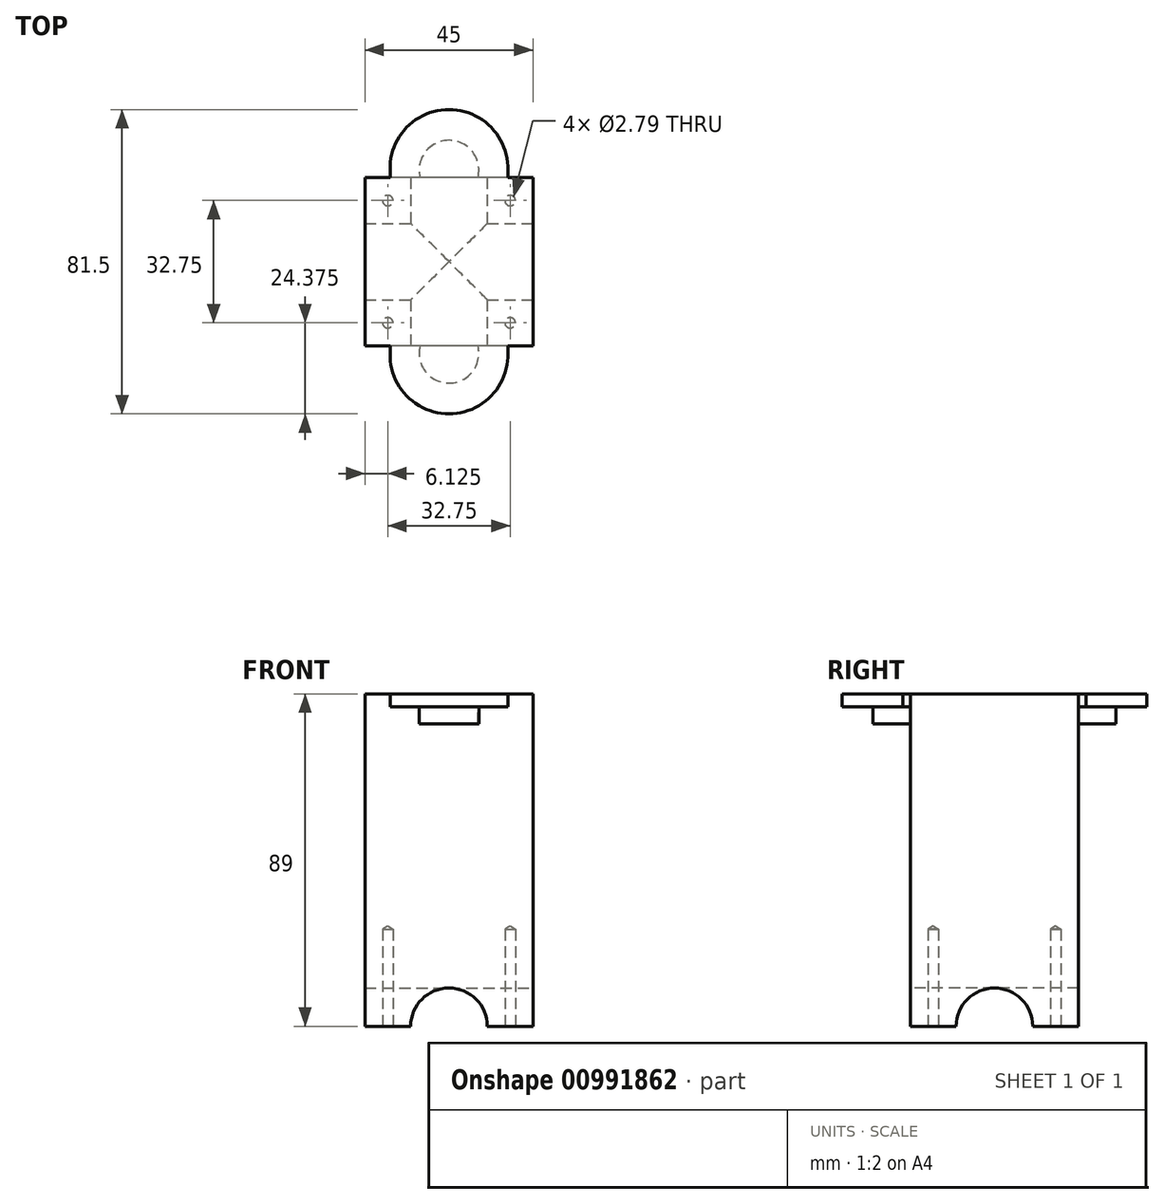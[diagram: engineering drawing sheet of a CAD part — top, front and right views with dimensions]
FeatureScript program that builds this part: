
annotation { "Feature Type Name" : "Feature", "Feature Type Description" : "" }
export const myFeature = defineFeature(function(context is Context, id is Id, definition is map)
    precondition{}
    {
        {
            var Q0;
            Q0=qCreatedBy(makeId("Top.planeOp"),FACE);
            var sketch = newSketch(context, id + "F0", { "sketchPlane" : qUnion([Q0])});
            skLineSegment(sketch, "E0.bottom", {"start": v(22.5, -22.5) * mm, "end": v(-22.5, -22.5) * mm});
            skLineSegment(sketch, "E0.top", {"start": v(22.5, 22.5) * mm, "end": v(-22.5, 22.5) * mm});
            skLineSegment(sketch, "E0.left", {"start": v(22.5, -22.5) * mm, "end": v(22.5, 22.5) * mm});
            skLineSegment(sketch, "E0.right", {"start": v(-22.5, -22.5) * mm, "end": v(-22.5, 22.5) * mm});
            skPoint(sketch, "E0.middle", {"position": v(0, 0) * mm});
            skSolve(sketch);
        }
        {
            var Q0;
            Q0 = qSketchRegion(id + "F0", true);
            extrude(context, id + "F1", {"entities" : qUnion([Q0]), "depth" : 89 * mm, "offsetDistance" : 25 * mm});
        }
        {
            var Q0;
            Q0=qCreatedBy(makeId("Front.planeOp"),FACE);
            var sketch = newSketch(context, id + "F2", { "sketchPlane" : qUnion([Q0])});
            skCircle(sketch, "E1", {"center": v(0, 0) * mm, "radius": 10.25 * mm});
            skSolve(sketch);
        }
        {
            var Q0;
            Q0 = qSketchRegion(id + "F2", true);
            extrude(context, id + "F3", {"entities" : qUnion([Q0]), "operationType" : NewBodyOperationType.REMOVE, "oppositeDirection" : true, "depth" : 50 * mm, "offsetDistance" : 25 * mm, "symmetric" : true});
        }
        {
            var Q0;
            Q0=qCreatedBy(makeId("Right.planeOp"),FACE);
            var sketch = newSketch(context, id + "F4", { "sketchPlane" : qUnion([Q0])});
            skCircle(sketch, "E2", {"center": v(0, 0) * mm, "radius": 10.25 * mm});
            skSolve(sketch);
        }
        {
            var Q0;
            Q0 = qSketchRegion(id + "F4", true);
            extrude(context, id + "F5", {"entities" : qUnion([Q0]), "operationType" : NewBodyOperationType.REMOVE, "oppositeDirection" : true, "depth" : 55 * mm, "offsetDistance" : 25 * mm, "symmetric" : true});
        }
        {
            var Q0;
            Q0=makeQuery(id+"F1.opExtrude","CAP_FACE",FACE,{"disambiguationData":[OSD([sQuery(id+"F0.wireOp",EDGE,"E0.bottom"),sQuery(id+"F0.wireOp",EDGE,"E0.top"),sQuery(id+"F0.wireOp",EDGE,"E0.left"),sQuery(id+"F0.wireOp",EDGE,"E0.right")])],"isStart":false});
            var sketch = newSketch(context, id + "F6", { "sketchPlane" : qUnion([Q0])});
            skCircle(sketch, "E3", {"center": v(0, 25) * mm, "radius": 15.75 * mm});
            skCircle(sketch, "E4", {"center": v(0, -25) * mm, "radius": 15.75 * mm});
            skSolve(sketch);
        }
        {
            var Q0;
            Q0 = qSketchRegion(id + "F6", true);
            extrude(context, id + "F7", {"entities" : qUnion([Q0]), "operationType" : NewBodyOperationType.ADD, "oppositeDirection" : true, "depth" : 3.5 * mm, "offsetDistance" : 25 * mm});
        }
        {
            var Q0;
            {var subQ0=sQuery(id+"F0.wireOp",EDGE,"E0.bottom");var subQ1=makeQuery(id+"F1.opExtrude","SWEPT_FACE",FACE,{"disambiguationData":[OSD([subQ0])]});var subQ3=sQuery(id+"F0.wireOp",EDGE,"E0.left");var subQ4=makeQuery(id+"F1.opExtrude","SWEPT_FACE",FACE,{"disambiguationData":[OSD([subQ3])]});var subQ5=sQuery(id+"F0.wireOp",EDGE,"E0.top");Q0=makeQuery(id+"F5.boolean.opBoolean","SPLIT",FACE,{"disambiguationData":[TD([subQ1])],"derivedFrom":makeQuery(id+"F3.boolean.opBoolean","SPLIT",FACE,{"disambiguationData":[TD([subQ4])],"derivedFrom":makeQuery(id+"F1.opExtrude","CAP_FACE",FACE,{"disambiguationData":[OSD([subQ0,subQ5,subQ3,sQuery(id+"F0.wireOp",EDGE,"E0.right")])],"isStart":true})})});}
            var sketch = newSketch(context, id + "F8", { "sketchPlane" : qUnion([Q0])});
            skPoint(sketch, "E5", {"position": v(16.38, 16.38) * mm});
            skPoint(sketch, "E6", {"position": v(16.38, -16.38) * mm});
            skPoint(sketch, "E7", {"position": v(-16.38, 16.38) * mm});
            skPoint(sketch, "E8", {"position": v(-16.38, -16.38) * mm});
            skSolve(sketch);
        }
        {
            var Q0;
            Q0=sQuery(id+"F8.wireOp",VERTEX,"E5");
            var Q1;
            Q1=makeQuery(id+"F1.opExtrude","SWEPT_BODY",BODY,{"disambiguationData":[OSD([sQuery(id+"F0.wireOp",EDGE,"E0.bottom"),sQuery(id+"F0.wireOp",EDGE,"E0.top"),sQuery(id+"F0.wireOp",EDGE,"E0.left"),sQuery(id+"F0.wireOp",EDGE,"E0.right")])]});
            hole(context, id + "F9", {"style" : HoleStyle.SIMPLE, "endStyle" : HoleEndStyle.BLIND, "holeDiameter" : 2.8 * mm, "majorDiameter" : 5 * mm, "holeDepth" : 26 * mm, "isTappedThrough" : true, "tappedDepth" : 12 * mm, "tapClearance" : 3, "locations" : qUnion([Q0]), "scope" : qUnion([Q1])});
        }
        {
            var Q0;
            Q0=qCreatedBy(makeId("Top.planeOp"),FACE);
            var sketch = newSketch(context, id + "F10", { "sketchPlane" : qUnion([Q0])});
            skPoint(sketch, "E9", {"position": v(16.38, 16.38) * mm});
            skPoint(sketch, "E10", {"position": v(16.38, -16.38) * mm});
            skPoint(sketch, "E11", {"position": v(-16.38, 16.38) * mm});
            skPoint(sketch, "E12", {"position": v(-16.38, -16.38) * mm});
            skSolve(sketch);
        }
        {
            var Q0;
            Q0=qCreatedBy(makeId("Top.planeOp"),FACE);
            var sketch = newSketch(context, id + "F11", { "sketchPlane" : qUnion([Q0])});
            skPoint(sketch, "E13", {"position": v(16.38, 16.38) * mm});
            skPoint(sketch, "E14", {"position": v(16.38, -16.38) * mm});
            skPoint(sketch, "E15", {"position": v(-16.38, 16.38) * mm});
            skPoint(sketch, "E16", {"position": v(-16.38, -16.38) * mm});
            skSolve(sketch);
        }
        {
            var Q0;
            Q0=qCreatedBy(makeId("Top.planeOp"),FACE);
            var sketch = newSketch(context, id + "F12", { "sketchPlane" : qUnion([Q0])});
            skPoint(sketch, "E17", {"position": v(16.38, 16.38) * mm});
            skPoint(sketch, "E18", {"position": v(16.38, -16.38) * mm});
            skPoint(sketch, "E19", {"position": v(-16.38, 16.38) * mm});
            skPoint(sketch, "E20", {"position": v(-16.38, -16.38) * mm});
            skSolve(sketch);
        }
        {
            var Q0;
            Q0=sQuery(id+"F10.wireOp",VERTEX,"E9");
            var Q1;
            Q1=makeQuery(id+"F1.opExtrude","SWEPT_BODY",BODY,{"disambiguationData":[OSD([sQuery(id+"F0.wireOp",EDGE,"E0.bottom"),sQuery(id+"F0.wireOp",EDGE,"E0.top"),sQuery(id+"F0.wireOp",EDGE,"E0.left"),sQuery(id+"F0.wireOp",EDGE,"E0.right")])]});
            hole(context, id + "F13", {"style" : HoleStyle.SIMPLE, "endStyle" : HoleEndStyle.BLIND, "oppositeDirection" : true, "holeDiameter" : 2.8 * mm, "majorDiameter" : 5 * mm, "holeDepth" : 26 * mm, "isTappedThrough" : true, "tappedDepth" : 12 * mm, "tapClearance" : 3, "locations" : qUnion([Q0]), "scope" : qUnion([Q1])});
        }
        {
            var Q0;
            Q0=sQuery(id+"F11.wireOp",VERTEX,"E15");
            var Q1;
            Q1=makeQuery(id+"F1.opExtrude","SWEPT_BODY",BODY,{"disambiguationData":[OSD([sQuery(id+"F0.wireOp",EDGE,"E0.bottom"),sQuery(id+"F0.wireOp",EDGE,"E0.top"),sQuery(id+"F0.wireOp",EDGE,"E0.left"),sQuery(id+"F0.wireOp",EDGE,"E0.right")])]});
            hole(context, id + "F14", {"style" : HoleStyle.SIMPLE, "endStyle" : HoleEndStyle.BLIND, "oppositeDirection" : true, "holeDiameter" : 2.8 * mm, "majorDiameter" : 5 * mm, "holeDepth" : 26 * mm, "isTappedThrough" : true, "tappedDepth" : 12 * mm, "tapClearance" : 3, "locations" : qUnion([Q0]), "scope" : qUnion([Q1])});
        }
        {
            var Q0;
            Q0=sQuery(id+"F12.wireOp",VERTEX,"E20");
            var Q1;
            Q1=makeQuery(id+"F1.opExtrude","SWEPT_BODY",BODY,{"disambiguationData":[OSD([sQuery(id+"F0.wireOp",EDGE,"E0.bottom"),sQuery(id+"F0.wireOp",EDGE,"E0.top"),sQuery(id+"F0.wireOp",EDGE,"E0.left"),sQuery(id+"F0.wireOp",EDGE,"E0.right")])]});
            hole(context, id + "F15", {"style" : HoleStyle.SIMPLE, "endStyle" : HoleEndStyle.BLIND, "oppositeDirection" : true, "holeDiameter" : 2.8 * mm, "majorDiameter" : 5 * mm, "holeDepth" : 26 * mm, "isTappedThrough" : true, "tappedDepth" : 12 * mm, "tapClearance" : 3, "locations" : qUnion([Q0]), "scope" : qUnion([Q1])});
        }
        {
            var Q0;
            Q0=makeQuery(id+"F7.boolean.opBoolean","MERGE",FACE,{"derivedFrom":[makeQuery(id+"F1.opExtrude","CAP_FACE",FACE,{"disambiguationData":[OSD([sQuery(id+"F0.wireOp",EDGE,"E0.bottom"),sQuery(id+"F0.wireOp",EDGE,"E0.top"),sQuery(id+"F0.wireOp",EDGE,"E0.left"),sQuery(id+"F0.wireOp",EDGE,"E0.right")])],"isStart":false}),makeQuery(id+"F7.opExtrude","CAP_FACE",FACE,{"disambiguationData":[OSD([sQuery(id+"F6.wireOp",EDGE,"E3")])],"isStart":true}),makeQuery(id+"F7.opExtrude","CAP_FACE",FACE,{"disambiguationData":[OSD([sQuery(id+"F6.wireOp",EDGE,"E4")])],"isStart":true})]});
            var sketch = newSketch(context, id + "F16", { "sketchPlane" : qUnion([Q0])});
            skLineSegment(sketch, "E21.bottom", {"start": v(15.75, -24.5) * mm, "end": v(-15.75, -24.5) * mm});
            skLineSegment(sketch, "E21.top", {"start": v(15.75, 24.5) * mm, "end": v(-15.75, 24.5) * mm});
            skLineSegment(sketch, "E21.left", {"start": v(15.75, -24.5) * mm, "end": v(15.75, 24.5) * mm});
            skLineSegment(sketch, "E21.right", {"start": v(-15.75, -24.5) * mm, "end": v(-15.75, 24.5) * mm});
            skPoint(sketch, "E21.middle", {"position": v(0, 0) * mm});
            skSolve(sketch);
        }
        {
            var Q0;
            Q0 = qSketchRegion(id + "F16", true);
            extrude(context, id + "F17", {"entities" : qUnion([Q0]), "operationType" : NewBodyOperationType.ADD, "oppositeDirection" : true, "depth" : 3.5 * mm, "offsetDistance" : 25 * mm});
        }
        {
            var Q0;
            Q0=makeQuery(id+"F17.boolean.opBoolean","MERGE",FACE,{"derivedFrom":[makeQuery(id+"F7.boolean.opBoolean","MERGE",FACE,{"derivedFrom":[makeQuery(id+"F1.opExtrude","CAP_FACE",FACE,{"disambiguationData":[OSD([sQuery(id+"F0.wireOp",EDGE,"E0.bottom"),sQuery(id+"F0.wireOp",EDGE,"E0.top"),sQuery(id+"F0.wireOp",EDGE,"E0.left"),sQuery(id+"F0.wireOp",EDGE,"E0.right")])],"isStart":false}),makeQuery(id+"F7.opExtrude","CAP_FACE",FACE,{"disambiguationData":[OSD([sQuery(id+"F6.wireOp",EDGE,"E3")])],"isStart":true}),makeQuery(id+"F7.opExtrude","CAP_FACE",FACE,{"disambiguationData":[OSD([sQuery(id+"F6.wireOp",EDGE,"E4")])],"isStart":true})]}),makeQuery(id+"F17.opExtrude","CAP_FACE",FACE,{"disambiguationData":[OSD([sQuery(id+"F16.wireOp",EDGE,"E21.bottom"),sQuery(id+"F16.wireOp",EDGE,"E21.top"),sQuery(id+"F16.wireOp",EDGE,"E21.left"),sQuery(id+"F16.wireOp",EDGE,"E21.right")])],"isStart":true})]});
            var sketch = newSketch(context, id + "F18", { "sketchPlane" : qUnion([Q0])});
            skCircle(sketch, "E22", {"center": v(0, 24.5) * mm, "radius": 8 * mm});
            skCircle(sketch, "E23", {"center": v(0, -24.5) * mm, "radius": 8 * mm});
            skSolve(sketch);
        }
        {
            var Q0;
            Q0 = qSketchRegion(id + "F18", true);
            extrude(context, id + "F19", {"entities" : qUnion([Q0]), "operationType" : NewBodyOperationType.ADD, "oppositeDirection" : true, "depth" : 8 * mm, "offsetDistance" : 25 * mm});
        }
    });
